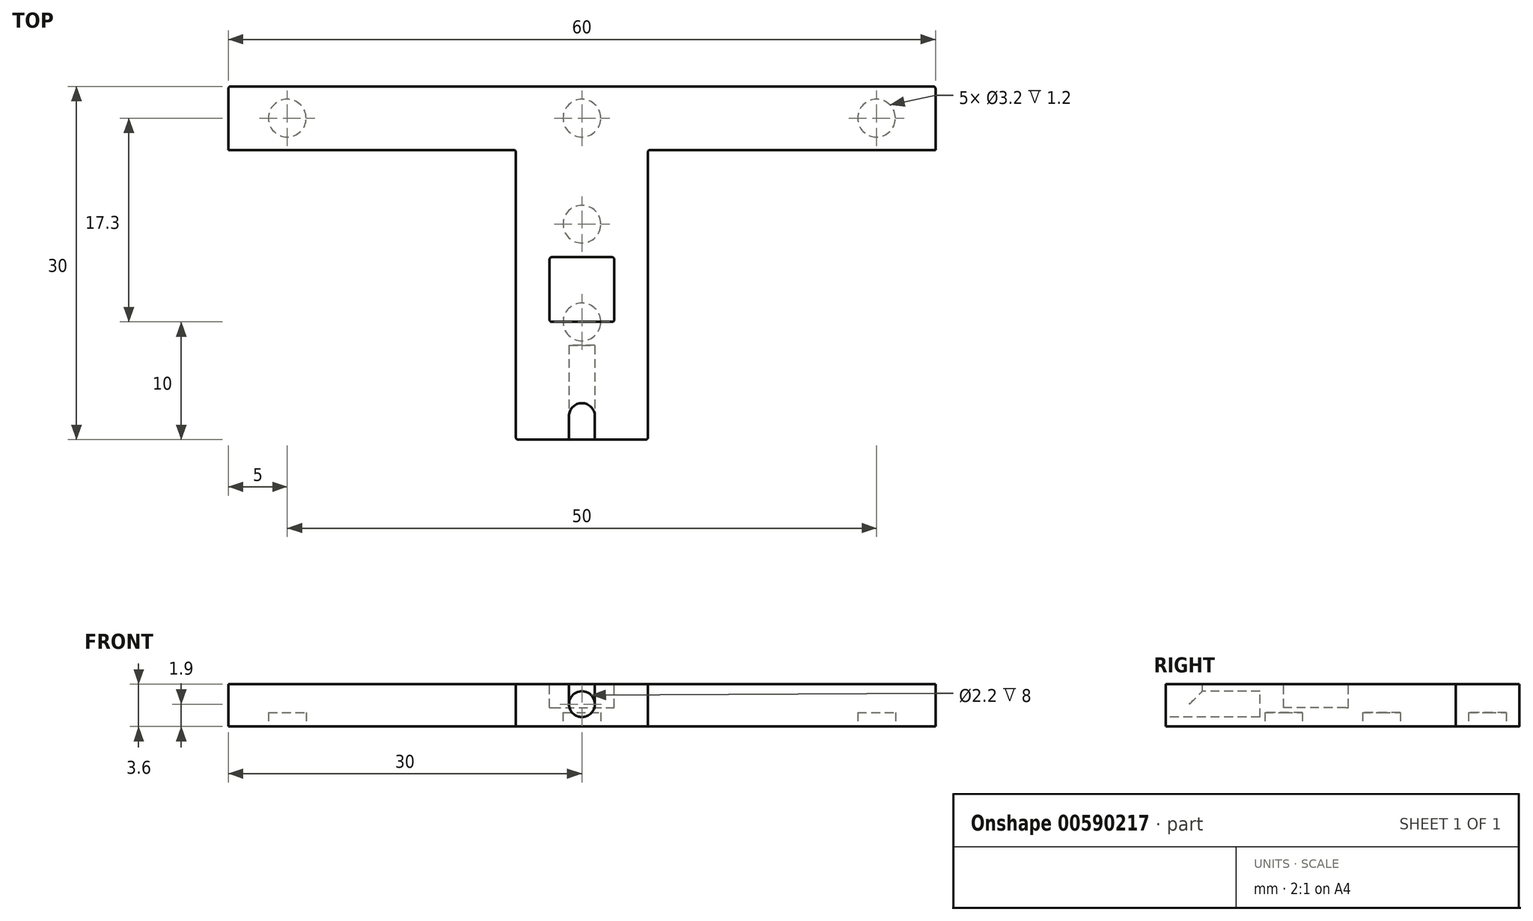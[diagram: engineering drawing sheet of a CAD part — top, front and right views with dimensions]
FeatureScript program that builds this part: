
annotation { "Feature Type Name" : "Feature", "Feature Type Description" : "" }
export const myFeature = defineFeature(function(context is Context, id is Id, definition is map)
    precondition{}
    {
        {
            var Q0;
            Q0=qCreatedBy(makeId("Top.planeOp"),FACE);
            var sketch = newSketch(context, id + "F0", { "sketchPlane" : qUnion([Q0])});
            skLineSegment(sketch, "E0.bottom", {"start": v(-30, 15) * mm, "end": v(30, 15) * mm});
            skLineSegment(sketch, "E0.top", {"start": v(-30, -15) * mm, "end": v(30, -15) * mm});
            skLineSegment(sketch, "E0.left", {"start": v(-30, 15) * mm, "end": v(-30, -15) * mm});
            skLineSegment(sketch, "E0.right", {"start": v(30, 15) * mm, "end": v(30, -15) * mm});
            skPoint(sketch, "E0.middle", {"position": v(0, 0) * mm});
            skLineSegment(sketch, "E1", {"start": v(-5.6, 9.6) * mm, "end": v(-5.6, -15) * mm});
            skLineSegment(sketch, "E2", {"start": v(5.6, 9.6) * mm, "end": v(5.6, -15) * mm});
            skLineSegment(sketch, "E3", {"start": v(-30, 9.6) * mm, "end": v(-5.6, 9.6) * mm});
            skLineSegment(sketch, "E4.trimOffspring", {"start": v(5.6, 9.6) * mm, "end": v(30, 9.6) * mm});
            skSolve(sketch);
        }
        {
            var Q0;
            {var subQ4=sQuery(id+"F0.wireOp",EDGE,"E0.bottom");Q0=makeQuery(id+"F0.imprint","IMPRINT",FACE,{"disambiguationData":[TD([[makeQuery(id+"F0.imprint","IMPRINT",EDGE,{"derivedFrom":subQ4}),-1.0]])]});}
            extrude(context, id + "F1", {"entities" : qUnion([Q0]), "depth" : 3.6 * mm, "offsetDistance" : 25 * mm});
        }
        {
            var Q0;
            Q0=makeQuery(id+"F1.opExtrude","SWEPT_FACE",FACE,{"disambiguationData":[OSD([sQuery(id+"F0.wireOp",EDGE,"E0.top")])]});
            var sketch = newSketch(context, id + "F2", { "sketchPlane" : qUnion([Q0])});
            skCircle(sketch, "E5", {"center": v(0, 1.9) * mm, "radius": 1.1 * mm});
            skSolve(sketch);
        }
        {
            var Q0;
            Q0 = qSketchRegion(id + "F2", true);
            extrude(context, id + "F3", {"entities" : qUnion([Q0]), "operationType" : NewBodyOperationType.REMOVE, "oppositeDirection" : true, "depth" : 8 * mm, "offsetDistance" : 25 * mm});
        }
        {
            var Q0;
            Q0=makeQuery(id+"F1.opExtrude","CAP_FACE",FACE,{"disambiguationData":[OSD([sQuery(id+"F0.wireOp",EDGE,"E0.bottom"),sQuery(id+"F0.wireOp",EDGE,"E0.top"),sQuery(id+"F0.wireOp",EDGE,"E0.left"),sQuery(id+"F0.wireOp",EDGE,"E0.right"),sQuery(id+"F0.wireOp",EDGE,"gsp4KYbM-J25M-Tdfx-hKmR-01IKLOIH4CFK"),sQuery(id+"F0.wireOp",EDGE,"E1"),sQuery(id+"F0.wireOp",EDGE,"N5Ual0gW-elwf-1orW-aHdQ-UR0eQ4HbNnas"),sQuery(id+"F0.wireOp",EDGE,"E2"),sQuery(id+"F0.wireOp",EDGE,"E3"),sQuery(id+"F0.wireOp",EDGE,"jmHPhk3V-i4O4-BE8z-YyfG-69C0470fCKaC"),sQuery(id+"F0.wireOp",EDGE,"8bff5e04-ab58-4aef-9016-863673a35b32.trimOffspring"),sQuery(id+"F0.wireOp",EDGE,"2f28dfef-9324-4829-89ef-fc651798a962.trimOffspring"),sQuery(id+"F0.wireOp",EDGE,"83b0df3e-3aae-4dab-9533-a2a7d92c7e0b.trimOffspring"),sQuery(id+"F0.wireOp",EDGE,"E4.trimOffspring")])],"isStart":false});
            var sketch = newSketch(context, id + "F4", { "sketchPlane" : qUnion([Q0])});
            skLineSegment(sketch, "E6.bottom", {"start": v(-1.1, -15) * mm, "end": v(1.1, -15) * mm});
            skLineSegment(sketch, "E6.top", {"start": v(-1.1, -13) * mm, "end": v(1.1, -13) * mm});
            skLineSegment(sketch, "E6.left", {"start": v(-1.1, -15) * mm, "end": v(-1.1, -13) * mm});
            skLineSegment(sketch, "E6.right", {"start": v(1.1, -15) * mm, "end": v(1.1, -13) * mm});
            skArc(sketch, "E7", {"start": v(1.1, -13) * mm, "mid": v(0, -11.9) * mm, "end": v(-1.1, -13) * mm});
            skSolve(sketch);
        }
        {
            var Q0;
            Q0 = qSketchRegion(id + "F4", true);
            extrude(context, id + "F5", {"entities" : qUnion([Q0]), "operationType" : NewBodyOperationType.REMOVE, "oppositeDirection" : true, "depth" : 1.7 * mm, "offsetDistance" : 25 * mm});
        }
        {
            var Q0;
            Q0=makeQuery(id+"F1.opExtrude","CAP_FACE",FACE,{"disambiguationData":[OSD([sQuery(id+"F0.wireOp",EDGE,"E0.bottom"),sQuery(id+"F0.wireOp",EDGE,"E0.top"),sQuery(id+"F0.wireOp",EDGE,"E0.left"),sQuery(id+"F0.wireOp",EDGE,"E0.right"),sQuery(id+"F0.wireOp",EDGE,"E1"),sQuery(id+"F0.wireOp",EDGE,"E2"),sQuery(id+"F0.wireOp",EDGE,"E3"),sQuery(id+"F0.wireOp",EDGE,"E4.trimOffspring")])],"isStart":true});
            var sketch = newSketch(context, id + "F6", { "sketchPlane" : qUnion([Q0])});
            skCircle(sketch, "E8", {"center": v(0, 5) * mm, "radius": 1.6 * mm});
            skCircle(sketch, "E9", {"center": v(0, -3.3) * mm, "radius": 1.6 * mm});
            skCircle(sketch, "E10", {"center": v(25, -12.3) * mm, "radius": 1.6 * mm});
            skCircle(sketch, "E11", {"center": v(-25, -12.3) * mm, "radius": 1.6 * mm});
            skCircle(sketch, "E12", {"center": v(0, -12.3) * mm, "radius": 1.6 * mm});
            skSolve(sketch);
        }
        {
            var Q0;
            Q0 = qSketchRegion(id + "F6", true);
            extrude(context, id + "F7", {"entities" : qUnion([Q0]), "operationType" : NewBodyOperationType.REMOVE, "oppositeDirection" : true, "depth" : 1.2 * mm, "offsetDistance" : 25 * mm});
        }
        {
            var Q0;
            Q0=makeQuery(id+"F1.opExtrude","CAP_FACE",FACE,{"disambiguationData":[OSD([sQuery(id+"F0.wireOp",EDGE,"E0.bottom"),sQuery(id+"F0.wireOp",EDGE,"E0.top"),sQuery(id+"F0.wireOp",EDGE,"E0.left"),sQuery(id+"F0.wireOp",EDGE,"E0.right"),sQuery(id+"F0.wireOp",EDGE,"E1"),sQuery(id+"F0.wireOp",EDGE,"E2"),sQuery(id+"F0.wireOp",EDGE,"E3"),sQuery(id+"F0.wireOp",EDGE,"E4.trimOffspring")])],"isStart":false});
            var sketch = newSketch(context, id + "F8", { "sketchPlane" : qUnion([Q0])});
            skLineSegment(sketch, "E13.bottom", {"start": v(-2.75, 0.5) * mm, "end": v(2.75, 0.5) * mm});
            skLineSegment(sketch, "E13.top", {"start": v(-2.75, -5) * mm, "end": v(2.75, -5) * mm});
            skLineSegment(sketch, "E13.left", {"start": v(-2.75, 0.5) * mm, "end": v(-2.75, -5) * mm});
            skLineSegment(sketch, "E13.right", {"start": v(2.75, 0.5) * mm, "end": v(2.75, -5) * mm});
            skPoint(sketch, "E13.middle", {"position": v(0, -2.25) * mm});
            skSolve(sketch);
        }
        {
            var Q0;
            Q0 = qSketchRegion(id + "F8", true);
            extrude(context, id + "F9", {"entities" : qUnion([Q0]), "operationType" : NewBodyOperationType.REMOVE, "oppositeDirection" : true, "depth" : 2 * mm, "offsetDistance" : 25 * mm});
        }
        {
            var Q0;
            Q0=makeQuery(id+"F1.opExtrude","SWEPT_EDGE",EDGE,{"disambiguationData":[OSD([sQuery(id+"F0.wireOp",EDGE,"gsp4KYbM-J25M-Tdfx-hKmR-01IKLOIH4CFK"),sQuery(id+"F0.wireOp",EDGE,"8bff5e04-ab58-4aef-9016-863673a35b32.trimOffspring")])]});
            var Q1;
            Q1=makeQuery(id+"F1.opExtrude","SWEPT_EDGE",EDGE,{"disambiguationData":[OSD([sQuery(id+"F0.wireOp",EDGE,"E1"),sQuery(id+"F0.wireOp",EDGE,"E3")])]});
            var Q2;
            Q2=makeQuery(id+"F1.opExtrude","SWEPT_EDGE",EDGE,{"disambiguationData":[OSD([sQuery(id+"F0.wireOp",EDGE,"E1"),sQuery(id+"F0.wireOp",EDGE,"jmHPhk3V-i4O4-BE8z-YyfG-69C0470fCKaC")])]});
            var Q3;
            Q3=makeQuery(id+"F1.opExtrude","SWEPT_EDGE",EDGE,{"disambiguationData":[OSD([sQuery(id+"F0.wireOp",EDGE,"N5Ual0gW-elwf-1orW-aHdQ-UR0eQ4HbNnas"),sQuery(id+"F0.wireOp",EDGE,"83b0df3e-3aae-4dab-9533-a2a7d92c7e0b.trimOffspring")])]});
            var Q4;
            Q4=makeQuery(id+"F1.opExtrude","SWEPT_EDGE",EDGE,{"disambiguationData":[OSD([sQuery(id+"F0.wireOp",EDGE,"E2"),sQuery(id+"F0.wireOp",EDGE,"E4.trimOffspring")])]});
            var Q5;
            Q5=makeQuery(id+"F1.opExtrude","SWEPT_EDGE",EDGE,{"disambiguationData":[OSD([sQuery(id+"F0.wireOp",EDGE,"E2"),sQuery(id+"F0.wireOp",EDGE,"2f28dfef-9324-4829-89ef-fc651798a962.trimOffspring")])]});
            var Q6;
            Q6=makeQuery(id+"F1.opExtrude","SWEPT_EDGE",EDGE,{"disambiguationData":[OSD([sQuery(id+"F0.wireOp",EDGE,"E0.bottom"),sQuery(id+"F0.wireOp",EDGE,"E0.right")])]});
            var Q7;
            Q7=makeQuery(id+"F1.opExtrude","SWEPT_EDGE",EDGE,{"disambiguationData":[OSD([sQuery(id+"F0.wireOp",EDGE,"E0.bottom"),sQuery(id+"F0.wireOp",EDGE,"E0.left")])]});
            var Q8;
            Q8=makeQuery(id+"F9.boolean.opBoolean","COPY",EDGE,{"derivedFrom":makeQuery(id+"F9.opExtrude","SWEPT_EDGE",EDGE,{"disambiguationData":[OSD([sQuery(id+"F8.wireOp",EDGE,"E13.bottom"),sQuery(id+"F8.wireOp",EDGE,"E13.left")])]})});
            var Q9;
            Q9=makeQuery(id+"F9.boolean.opBoolean","COPY",EDGE,{"derivedFrom":makeQuery(id+"F9.opExtrude","SWEPT_EDGE",EDGE,{"disambiguationData":[OSD([sQuery(id+"F8.wireOp",EDGE,"E13.bottom"),sQuery(id+"F8.wireOp",EDGE,"E13.right")])]})});
            var Q10;
            Q10=makeQuery(id+"F9.boolean.opBoolean","COPY",EDGE,{"derivedFrom":makeQuery(id+"F9.opExtrude","SWEPT_EDGE",EDGE,{"disambiguationData":[OSD([sQuery(id+"F8.wireOp",EDGE,"E13.top"),sQuery(id+"F8.wireOp",EDGE,"E13.right")])]})});
            var Q11;
            Q11=makeQuery(id+"F9.boolean.opBoolean","COPY",EDGE,{"derivedFrom":makeQuery(id+"F9.opExtrude","SWEPT_EDGE",EDGE,{"disambiguationData":[OSD([sQuery(id+"F8.wireOp",EDGE,"E13.top"),sQuery(id+"F8.wireOp",EDGE,"E13.left")])]})});
            fillet(context, id + "F10", {"entities" : qUnion([Q0, Q1, Q2, Q3, Q4, Q5, Q6, Q7, Q8, Q9, Q10, Q11]), "radius" : .2 * mm, "tangentPropagation" : true, "allowEdgeOverflow" : false});
        }
    });
